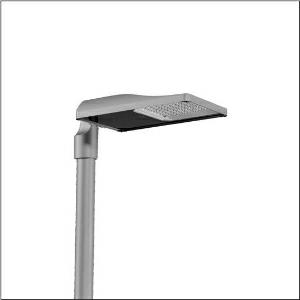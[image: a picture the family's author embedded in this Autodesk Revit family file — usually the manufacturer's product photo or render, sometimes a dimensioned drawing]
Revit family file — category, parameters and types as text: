
# Revit family: streetlight_sl_31_midi___pl52_5xh3h4aa08ma_de42
name_source: partatom
category: Lighting Fixtures
units: mm (PartAtom-declared; Revit-internal decimal feet)

## family parameters
Cut with Voids When Loaded = No
Host = Face
Light Source = No
Part Type = Normal
Room Calculation Point = No
Round Connector Dimension = Use Diameter
Shared = No

## types (1)
- --- (1 x LED, 19840 lm, 145.3 W, 4000K)
    Apparent Load = 145 VA
    CIE Flux Codes = 27 59 98 100 100
    Color Rendering = 70
    Color Temperature = 4000K
    Default Elevation = 1800 mm
    Description = Streetlight SL 31 midi Easy LST mast luminaire for post-top, side-entry; light control with lens of PMMA; light distribution: PL52, direct asymmetric distribution, for standard-compliant lighting for roads and squares; LED: luminous flux: 19.840lm, light colour: 740, colour temperature: 4000K; luminous efficacy: 136,5lm/W; control: pre-setting: linear dimming characteristic, flexible luminous flux parameterisation, time-dependent luminous flux control, constant luminous flux control, power reduction, intelligent temperature release in ECG and LED module, overheat protection; luminaire housing, of diecast aluminium, Siteco® metallic grey (DB 702S), corrosivity category C5 high according to DIN EN ISO 12944; cover of toughened safety glass, transparent, mast flange of diecast aluminium, Siteco® metallic grey (DB 702S), spigot size: 76/60mm, mast flange included unmounted; with cable H07RN-F 3x 1.5mm², cable length: 10,5m, connection cable pre-assembled; mains connection: 220..240V, AC, 50/60Hz; power consumption (at start of service life): 145,3W / (at end of service life): 161,8W / (with reduced operation 50%): 61,1W; protection rating (complete): IP66; insulation class (complete): insulation class II (safety insulation); impact resistance: IK10; certification: CE, ENEC, ENEC+, VDE, UKCA; permissible operating ambient temperature for outdoor applications: -40..+50°C; packaging unit: 1 piece

Light Distribution: PL52
    Height = 79 mm
    Lamp = 1 x LED
    Lamp Light Flux = 19840 lm
    Lamp Power = 145.3 W
    Lamp count = 1
    Length = 577 mm
    Luminous efficacy = 137 lm/W
    Manufacturer = Siteco
    ModVariant = No
    Model = 5XH3H4AA08MA
    Number of Poles = 1
    OnlyDefault = Yes
    Power Factor = 1
    Product Name = Streetlight SL 31 midi | PL52
    Product group = mast luminaire | pylon top
    ProductGroupID = 6100
    Protection Class = Protection class II
    Protection Degree = IP 66
    RLX_Detail_Level = 1
    RLX_Emergency_Light_Flux = 0 lm
    RLX_Emergency_Type = 0
    RLX_Emergency_Type_DB = No
    RlxData = <blob elided: 52353 chars, md5=6ee425fc>
    Socket = socket
    Standby Power = 0 W
    System Light Flux = 19841 lm
    System Power = 145 W
    Type Comments = factory setting: luminous flux: 100 % | dim-lin: 254 | 747 mA
    Type Image = l_1300317.jpg
    URL = http://relux.com
    VarID = @adj_063875
    Voltage = 0 V
    Weight = 0.00 kg
    Width = 362 mm

## geometry (parser evidence)
native form markers: Blend x4, Sweep x12
no freeform markers — native parametric forms only
